# Revit family: nachttischlampe
name_source: partatom
category: Leuchten
units: mm (PartAtom-declared; Revit-internal decimal feet)

## family parameters
Arbeitsebenenbasiert = Nein
Beim Laden mit Abzugskörper schneiden = Nein
Bemaßung runder Anschluss = Durchmesser verwenden
Beschriftungsausrichtung beibehalten = Nein
Gemeinsam genutzt = Nein
Immer vertikal = Ja
Lichtquelle = Ja
Raumberechnungspunkt = Nein
Teiletyp = Normal

## types (1)
- nachttischlampe
    Breite Fuß = 160 mm  [stored 0.524934 ft]
    Dicke Fuss = 6 mm  [stored 0.019685 ft]
    Farbfilter = 16777215
    Farbtemperaturverschiebung bei Dämpfen der Lampe = <Keine Auswahl>
    Größe des Lichtquellensymbols = 50 mm  [stored 0.164042 ft]
    H = 500 mm  [stored 1.64042 ft]
    Höhe Schirm = 200 mm  [stored 0.656168 ft]
    Lampenbasismaterial = Metall - Bronze
    Lampenschirmmaterial = Schirm - Beige, Texturiert
    Radius Schirm oben = 50 mm  [stored 0.164042 ft]
    Vorgabe-Ansicht = 0 mm  [stored 0 ft]
    Wandstärke Schirm = 5 mm  [stored 0.0164042 ft]

note: [stored X ft] marks values corroborated as IEEE doubles in the binary element streams (Revit-internal decimal feet)
